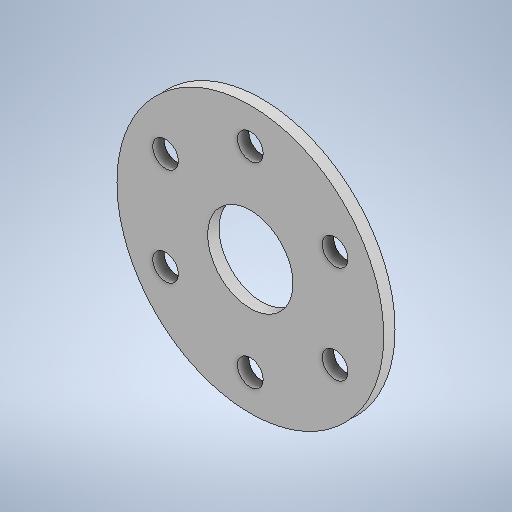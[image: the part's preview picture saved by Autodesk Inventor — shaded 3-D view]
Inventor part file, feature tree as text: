
AUTODESK INVENTOR PART (.ipt)
format: ipt  version: 2025.2 (Build 292293000, 293)  size: 244,224 bytes
history: native  units: mm
features: sketch x2, extrude x1
ambient origin geometry x8: Origin, YZ Plane, XZ Plane, XY Plane, X Axis, Y Axis, Z Axis, Center Point
bodies: Solid1 (feature_tree)
feature tree (3):
  extrude  "Extrusion1"  Depth=34.5mm
  sketch  "Sketch1"  dims[d0=47.0mm d1=34.5mm]
  sketch  "Sketch Circular Pattern1"  dims[d2=4.5mm d3=60.0mm d5=360.0deg d7=15.0mm d8=2.0mm d9=0.0mm]
